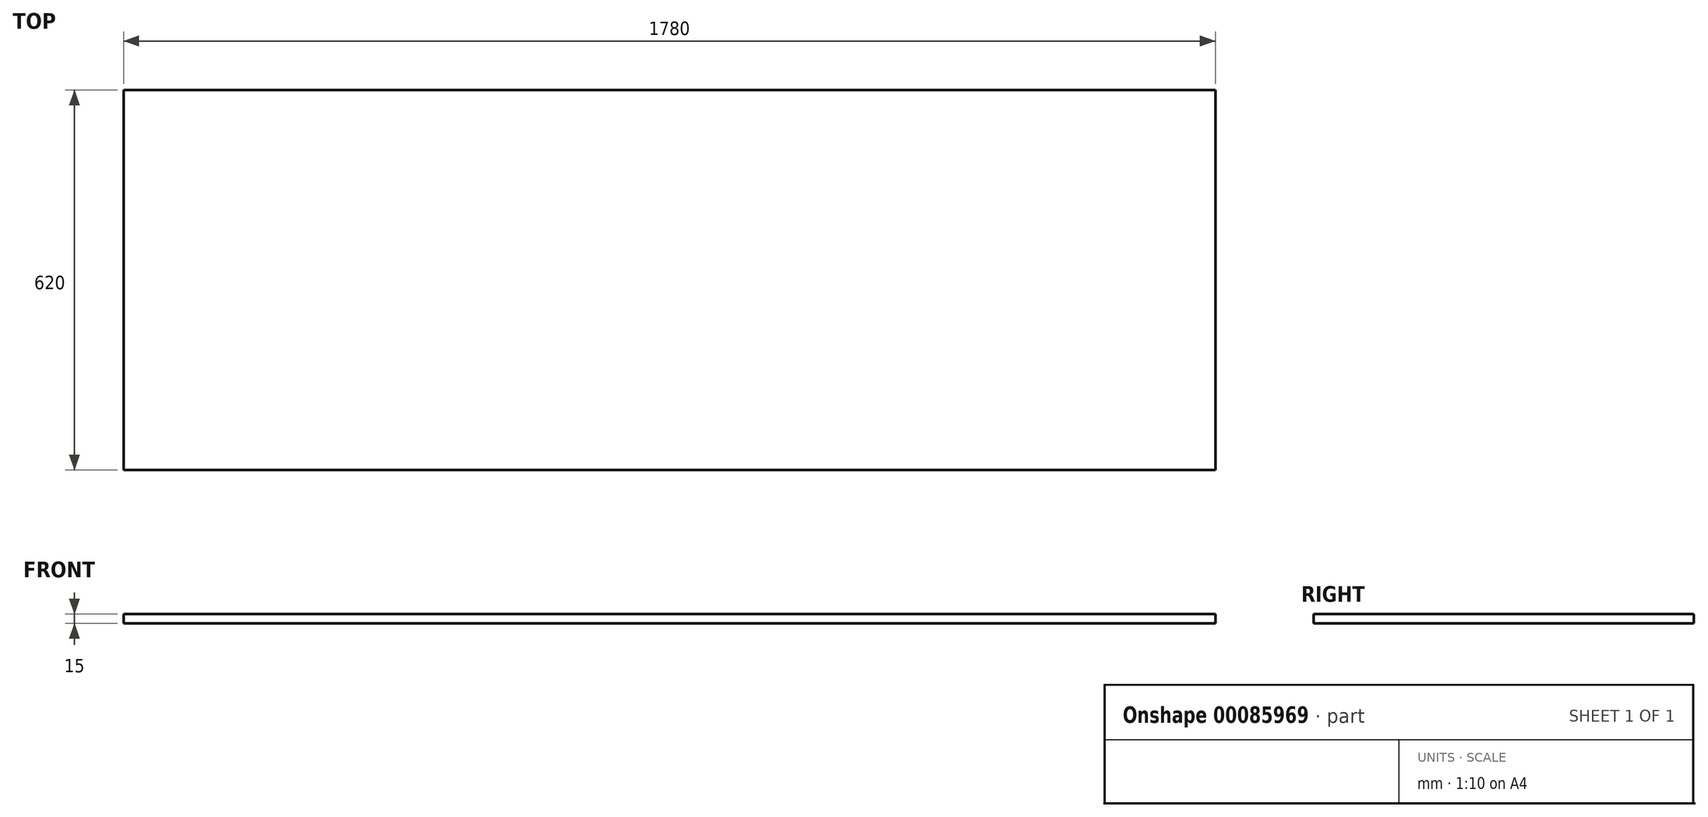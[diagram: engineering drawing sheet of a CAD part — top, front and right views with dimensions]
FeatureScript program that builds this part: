
annotation { "Feature Type Name" : "Feature", "Feature Type Description" : "" }
export const myFeature = defineFeature(function(context is Context, id is Id, definition is map)
    precondition{}
    {
        {
            var Q0;
            Q0=qCreatedBy(makeId("Top.planeOp"),FACE);
            var sketch = newSketch(context, id + "F0", { "sketchPlane" : qUnion([Q0])});
            skLineSegment(sketch, "E0", {"start": v(0, 0) * mm, "end": v(1780, 0) * mm});
            skLineSegment(sketch, "E1", {"start": v(1780, 0) * mm, "end": v(1780, 620) * mm});
            skLineSegment(sketch, "E2", {"start": v(1780, 620) * mm, "end": v(0, 620) * mm});
            skLineSegment(sketch, "E3", {"start": v(0, 620) * mm, "end": v(0, 0) * mm});
            skSolve(sketch);
        }
        {
            var Q0;
            Q0=makeQuery(id+"F0.imprint","IMPRINT",FACE,{"disambiguationData":[TD([[makeQuery(id+"F0.imprint","IMPRINT",EDGE,{"derivedFrom":sQuery(id+"F0.wireOp",EDGE,"E0")}),1.0]])]});
            extrude(context, id + "F1", {"entities" : qUnion([Q0]), "depth" : 15 * mm});
        }
    });
